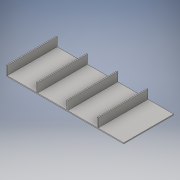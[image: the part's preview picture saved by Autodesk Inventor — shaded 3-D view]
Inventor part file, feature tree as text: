
AUTODESK INVENTOR PART (.ipt)
format: ipt  version: 2016 (Build 200138000, 138)  size: 135,168 bytes
history: native  units: in
note: dims shown in document units (in); Inventor stores cm internally (conversion verified against a paired STEP export)
features: extrude x5, sketch x5
ambient origin geometry x8: Origin, YZ Plane, XZ Plane, XY Plane, X Axis, Y Axis, Z Axis, Center Point
bodies: Solid1 (feature_tree)
feature tree (10):
  extrude  "Extrusion1"  Depth=0.063in
  extrude  "Extrusion2"  Depth=0.063in
  extrude  "Extrusion3"  Depth=0.063in
  extrude  "Extrusion4"  Depth=0.063in
  extrude  "Extrusion5"  Depth=0.063in
  sketch  "Sketch1"  dims[d0=8.0in d1=0.063in]
  sketch  "Sketch2"  dims[d2=3.4in d3=0.0in d4=0.063in]
  sketch  "Sketch3"  dims[d5=0.6in d6=0.0in d7=0.063in]
  sketch  "Sketch4"  dims[d8=0.6in d9=0.0in d10=0.063in]
  sketch  "Sketch5"  dims[d11=0.6in d12=0.0in d13=0.063in d14=0.6in d15=0.0in]
